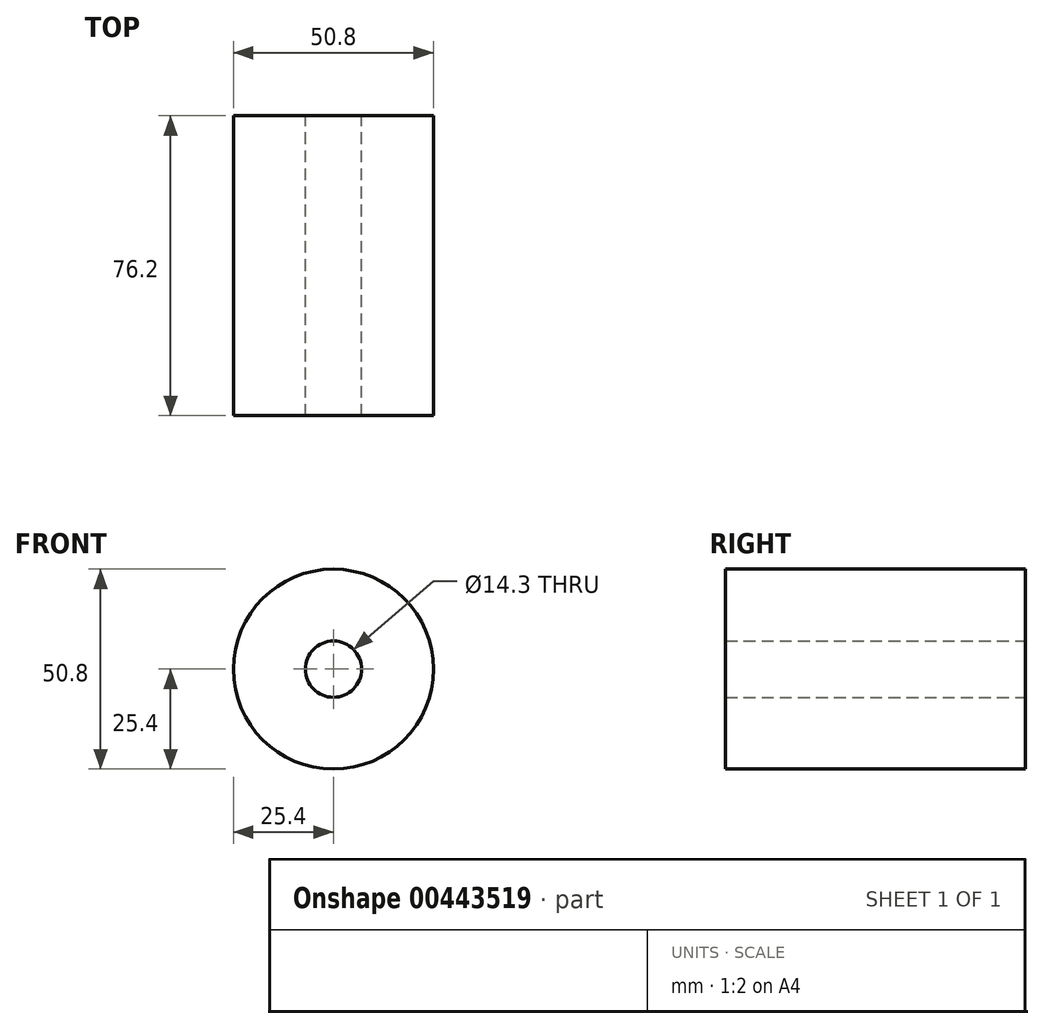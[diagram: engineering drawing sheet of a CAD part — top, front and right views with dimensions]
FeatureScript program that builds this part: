
annotation { "Feature Type Name" : "Feature", "Feature Type Description" : "" }
export const myFeature = defineFeature(function(context is Context, id is Id, definition is map)
    precondition{}
    {
        {
            var Q0;
            Q0=qCreatedBy(makeId("Right.planeOp"),FACE);
            var sketch = newSketch(context, id + "F0", { "sketchPlane" : qUnion([Q0])});
            skCircle(sketch, "E0", {"center": v(0, 0) * mm, "radius": 25.4 * mm});
            skCircle(sketch, "E1", {"center": v(0, 0) * mm, "radius": 7.15 * mm});
            skSolve(sketch);
        }
        {
            var Q0;
            Q0=makeQuery(id+"F0.imprint","IMPRINT",FACE,{"disambiguationData":[TD([[makeQuery(id+"F0.imprint","IMPRINT",EDGE,{"derivedFrom":sQuery(id+"F0.wireOp",EDGE,"E0")}),1.0]])]});
            extrude(context, id + "F1", {"entities" : qUnion([Q0]), "depth" : 76.2 * mm});
        }
        {
            var Q0;
            Q0=makeQuery(id+"F1.opExtrude","SWEPT_BODY",BODY,{"disambiguationData":[OSD([sQuery(id+"F0.wireOp",EDGE,"E0"),sQuery(id+"F0.wireOp",EDGE,"E1")])]});
            deleteBodies(context, id + "F2", {"entities" : qUnion([Q0])});
        }
        {
            var Q0;
            Q0=qCreatedBy(makeId("Front.planeOp"),FACE);
            var sketch = newSketch(context, id + "F3", { "sketchPlane" : qUnion([Q0])});
            skCircle(sketch, "E2", {"center": v(0, 0) * mm, "radius": 25.4 * mm});
            skCircle(sketch, "E3", {"center": v(0, 0) * mm, "radius": 7.15 * mm});
            skSolve(sketch);
        }
        {
            var Q0;
            Q0=makeQuery(id+"F3.imprint","IMPRINT",FACE,{"disambiguationData":[TD([[makeQuery(id+"F3.imprint","IMPRINT",EDGE,{"derivedFrom":sQuery(id+"F3.wireOp",EDGE,"E2")}),1.0]])]});
            extrude(context, id + "F4", {"entities" : qUnion([Q0]), "depth" : 76.2 * mm});
        }
    });
